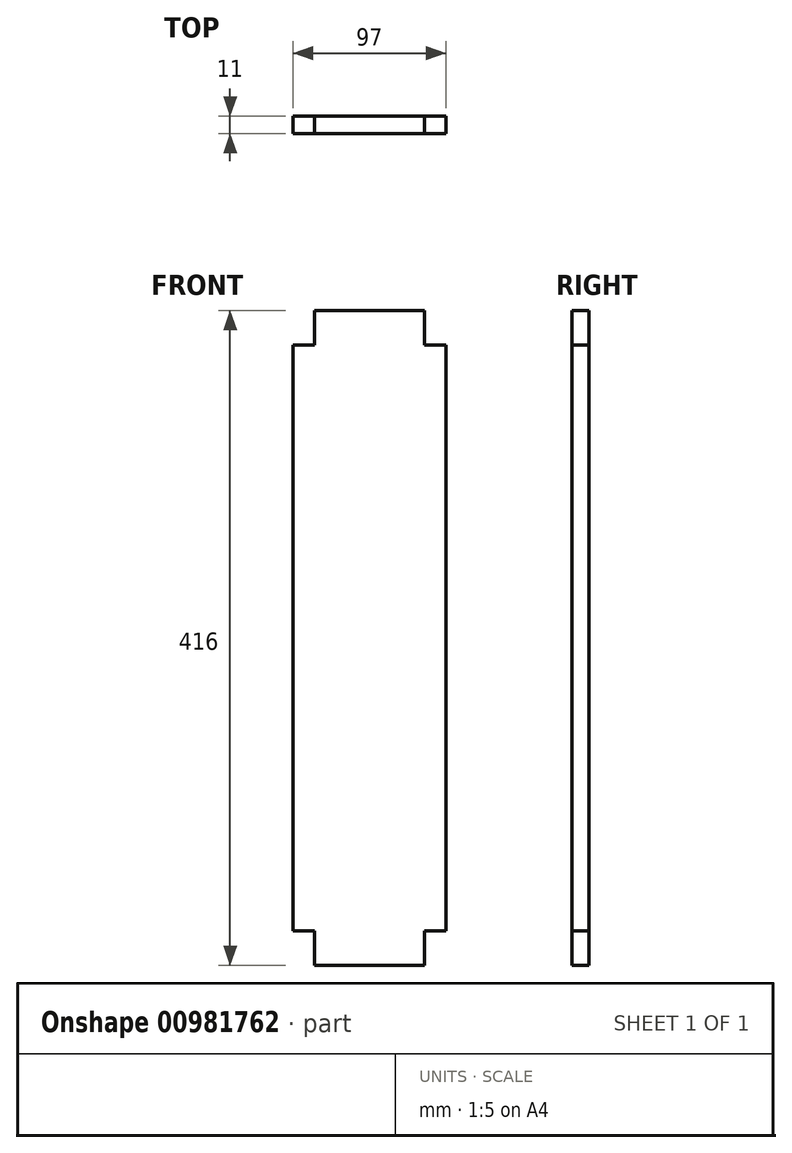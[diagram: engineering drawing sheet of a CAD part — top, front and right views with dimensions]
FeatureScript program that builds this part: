
annotation { "Feature Type Name" : "Feature", "Feature Type Description" : "" }
export const myFeature = defineFeature(function(context is Context, id is Id, definition is map)
    precondition{}
    {
        {
            var Q0;
            Q0=qCreatedBy(makeId("Front.planeOp"),FACE);
            var sketch = newSketch(context, id + "F0", { "sketchPlane" : qUnion([Q0])});
            skLineSegment(sketch, "E0", {"start": v(-48.5, 186) * mm, "end": v(-35, 186) * mm});
            skLineSegment(sketch, "E1", {"start": v(35, 186) * mm, "end": v(48.5, 186) * mm});
            skLineSegment(sketch, "E2", {"start": v(-48.5, -186) * mm, "end": v(-35, -186) * mm});
            skLineSegment(sketch, "E3", {"start": v(35, -186) * mm, "end": v(48.5, -186) * mm});
            skLineSegment(sketch, "E4", {"start": v(-48.5, 186) * mm, "end": v(-48.5, -186) * mm});
            skLineSegment(sketch, "E5", {"start": v(48.5, 186) * mm, "end": v(48.5, -186) * mm});
            skLineSegment(sketch, "E6", {"start": v(35, 208) * mm, "end": v(35, 186) * mm});
            skLineSegment(sketch, "E7", {"start": v(-35, 186) * mm, "end": v(-35, 208) * mm});
            skLineSegment(sketch, "E8", {"start": v(-35, 208) * mm, "end": v(35, 208) * mm});
            skLineSegment(sketch, "E9", {"start": v(-35, -186) * mm, "end": v(-35, -208) * mm});
            skLineSegment(sketch, "E10", {"start": v(-35, -208) * mm, "end": v(35, -208) * mm});
            skLineSegment(sketch, "E11", {"start": v(35, -186) * mm, "end": v(35, -208) * mm});
            skSolve(sketch);
        }
        {
            var Q0;
            Q0=makeQuery(id+"F0.imprint","IMPRINT",FACE,{"disambiguationData":[TD([[makeQuery(id+"F0.imprint","IMPRINT",EDGE,{"derivedFrom":sQuery(id+"F0.wireOp",EDGE,"E0")}),-1.0]])]});
            extrude(context, id + "F1", {"entities" : qUnion([Q0]), "depth" : 11 * mm, "offsetDistance" : 25 * mm});
        }
    });
